# Revit family: O2.5UMA-NRG_Meal Kit
name_source: partatom
category: Mechanical Equipment
revit_build: Autodesk Revit 2017 (Build: 20171027_0315(x64)
units: mm (PartAtom-declared; Revit-internal decimal feet)

## family parameters
Always vertical = Yes
Cut with Voids When Loaded = No
OmniClass Number = 23.40.40.11.17
OmniClass Title = Refrigerated Cases
Part Type = Normal
Room Calculation Point = No
Round Connector Dimension = Use Radius
Shared = No
Work Plane-Based = Yes

## types (37) — shared parameters
11" BF = Yes
ANTI SWEAT APPARENT LOAD = 0 VA
ANTI SWEAT HEATER AMPS = 0 A
ANTI SWEAT HEATER WATTAGE = 0 W
BASE HEIGHT = 5 1/8"
BTU PER FOOT CONVENTIONAL = 857
BTU PER FOOT PARALLEL = 750
CERTIFICATIONS = NSF 7, UL471, CSA
COIL REFRIGERATION CHARGE = 0.00 lb
CONTROL TYPE = T-STAT
DATE = 07/26/12
DEDICATED CIRCUIT = YES
DEFROST AMPS = 0 A
DEFROST PHASE = 1
DEFROST TIME AND DURATION = 2 @ 60 MIN
DEFROST WATTAGE = 0 W
DIEBOARD HEIGHT = 0"
DISCHARGE AIR TEMPERATURE = 31 °F
DRAIN LINE DIAMETER = 2"
DRAIN LINE RADIUS = 1"
DRAIN PIPE TYPE = PVC
DRIP PAN PLUMB TYPE = HARD
Default Elevation = 48"
Defrosts Per Day = 6
Description = MULTI DECK MERCHANDISER WITH SYNERG-E
Discharge Air Velocity (FPM) = 180 FPM
ELECTRIC DEFROST = No
ELECTRICAL DEFROST VOLTAGE = 0 V
EVAPORATOR TEMPERATURE = 28 °F
FAN AMPS = 0 A
FAN NUMBER OF POLES = 1
FAN TYPE = ECM
GROUND FAULT PROTECTION = NO
HEIGHT = 44 1/8"
HOT GAS DEFROST = No
High Efficiency Amps = 0 A
High Power (Cornice) Amps = 0 A
ISOLATED GROUND REQUIRED = NO
Keynote = DAIRY/DELI/MEAT/PRODUCE/SEAFOOD
LED LIGHTING AMPS PER ROW = 0 A
LIGHT TYPE = T8 FLUORESCENT
LIGHTING NUMBER OF POLES = 1
LIQUID LINE DIAMETER = 0"
LIQUID LINE RADIUS = 0"
Manufacturer = HILL PHOENIX
NUMBER OF WIRES = 3
PHASE = 1
POWER FACTOR = 1
PRESSURE REGULATOR = 0.00 psi
RECEPTICAL MOUNTING HEIGHT ABOVE FLOOR = 19 3/4"
REF PLANE FRONT BACK = 21 5/8"
REVERSE AIR DEFROST = No
SET BACK MODE FOR ENERGY CONSERVATION = NO
SHELVE 1 = Yes
SIZE OF COLD WATER HOOK UP = 0"
SIZE OF HOT WATER HOOK-UP = 0"
SUCTION LINE DIAMETER = 1"
SUCTION LINE RADIUS = 0"
Standard Power Amps = 0 A
Superheat Set Point @ Bulb (°F) = 6-8
T8 LIGHT OR LED LIGHT = Yes
TIME OFF DEFROST = Yes
TOEKICK HEIGHT = 5 1/2"
TOEKICK INSET = 1 1/2"
Timed-Off Defrost Fail-Safe (Min) = 30
Timed-Off Defrost Termination Temp = 42 °F
URL = http://www.hillphoenix.com
VOLTAGE = 120 V
WATER LINE MOUNTING HEIGHT ABOVE FLOOR = 0"
WEIGHT = 0.00 lb
WIDTH = 43 1/4"
zero-valued in all types: CORNICE AND NOSE LIGHT ROWS

## per-type parameters (varying)
- 04'-O2.5UMA-NRG-Dairy/Deli/Produce: 5" BF=No; Application Discipline=Meat; BLACK WHEELS=BLACK; BTU ADD FOR LIGHTS=368; BTU ADD PER SHELF PER FOOT=92; BTUH Conventional=847; BTUH Parallel=740; CONVENTIONAL EVAPORATOR LOAD=3796; DRAIN PIPE LENGTH=12"; Discharge Air (°F)=30 °F; EQUIPMENT MARK=O2.5UMA-NRG; Evaporator (°F)=26 °F; FAN AND ANTI SWEAT HEATER APPARENT LOAD=19 VA; FAN APPARENT LOAD=19 VA; FAN QUANTITY=1; FAN WATTAGE=11 W; Front Sill Height=Extended; High Efficiency Watts=11 W; High Power (Cornice) Watts=15 W; LED LIGHTING AMPS=0 A; LED LIGHTING BTU ADD PER ROW=36; LED LIGHTING WATTAGE=12 W; LEGEND NUMBER=O2.5UMA-NRG; LENGTH=48"; LENGTH FOR BTU=4; LIGHT AMPS=0 A; LIGHTING APPARENT LOAD=28 VA; LIGHTING WATTAGE=28 VA; Light Length=4'; Lights Per Row=1; Model=O2.5UMA-NRG; Number of Fans=1; PARALLEL EVAPORATOR LOAD=3368; REF PIPE LENGTH=22 3/4"; REF PLANE LEFT RIGHT=24"; SHELF LIGHT ROWS=1; SHELVE 2=No; SHELVE 3=No; SHELVE LENGTH=48"; Standard Power Watts=6 W; T8 LIGHTING AMPS=0 A; T8 LIGHTING AMPS PER ROW=0 A; T8 LIGHTING BTU ADD PER ROW=92; T8 LIGHTING WATTAGE=28 W; TOTAL APPARENT FAN-LIGHT AND A/S LOAD=39 VA; TOTAL CASE AMPS=0 A; TOTAL CASE WATTAGE=39 W
- 06': 5" BF=Yes; Application Discipline=Dairy/Deli/Produce; BLACK WHEELS=<By Category>; BTU ADD FOR LIGHTS=828; BTU ADD PER SHELF PER FOOT=69; BTUH Conventional=858; BTUH Parallel=750; CONVENTIONAL EVAPORATOR LOAD=5970; DRAIN LINE CONNECTION=Drain Connection; DRAIN PIPE LENGTH=0"; Discharge Air (°F)=31 °F; EQUIPMENT MARK=O2.5UMA-NRG; Evaporator (°F)=28 °F; FAN AND ANTI SWEAT HEATER APPARENT LOAD=38 VA; FAN APPARENT LOAD=38 VA; FAN CONNECTOR DESCRIPTION=FAN AND ANTI SWEAT CONNECTOR; FAN QUANTITY=2; FAN WATTAGE=22 W; Front Sill Height=All; High Efficiency Watts=22 W; High Power (Cornice) Watts=24 W; LED LIGHTING AMPS=0 A; LED LIGHTING BTU ADD PER ROW=27; LED LIGHTING WATTAGE=34 W; LEGEND NUMBER=O2.5UMA-NRG; LENGTH=72"; LENGTH FOR BTU=6; LIGHT AMPS=1 A; LIGHTING APPARENT LOAD=89 VA; LIGHTING CONNECTION DESCRIPTION=LIGHTING CONNECTOR; LIGHTING WATTAGE=89 VA; LIQUID LINE CONNECTION=LIQUID LINE CONNECTION; Light Length=3'; Lights Per Row=2; Model=O2.5UMA-NRG; Number of Fans=2; PARALLEL EVAPORATOR LOAD=5328; REF PIPE LENGTH=28 5/8"; REF PLANE LEFT RIGHT=36"; SHELF LIGHT ROWS=2; SHELVE 2=No; SHELVE 3=Yes; SHELVE LENGTH=36"; SUCTION LINE CONNECTION=SUCTION LINE CONNECTION; Standard Power Watts=9 W; T8 LIGHTING AMPS=1 A; T8 LIGHTING AMPS PER ROW=0 A; T8 LIGHTING BTU ADD PER ROW=69; T8 LIGHTING WATTAGE=89 W; TOTAL APPARENT FAN-LIGHT AND A/S LOAD=111 VA; TOTAL CASE AMPS=1 A; TOTAL CASE WATTAGE=111 W
- 06'-O2.5UMA-NRG- Meat: 5" BF=Yes; Application Discipline=Meat; BLACK WHEELS=<By Category>; BTU ADD FOR LIGHTS=828; BTU ADD PER SHELF PER FOOT=69; BTUH Conventional=847; BTUH Parallel=740; CONVENTIONAL EVAPORATOR LOAD=5970; DRAIN LINE CONNECTION=Drain Connection; DRAIN PIPE LENGTH=0"; Discharge Air (°F)=30 °F; EQUIPMENT MARK=O2.5UMA-NRG; Evaporator (°F)=26 °F; FAN AND ANTI SWEAT HEATER APPARENT LOAD=38 VA; FAN APPARENT LOAD=38 VA; FAN CONNECTOR DESCRIPTION=FAN AND ANTI SWEAT CONNECTOR; FAN QUANTITY=2; FAN WATTAGE=22 W; Front Sill Height=Extended; High Efficiency Watts=22 W; High Power (Cornice) Watts=24 W; LED LIGHTING AMPS=0 A; LED LIGHTING BTU ADD PER ROW=27; LED LIGHTING WATTAGE=34 W; LEGEND NUMBER=O2.5UMA-NRG; LENGTH=72"; LENGTH FOR BTU=6; LIGHT AMPS=1 A; LIGHTING APPARENT LOAD=89 VA; LIGHTING CONNECTION DESCRIPTION=LIGHTING CONNECTOR; LIGHTING WATTAGE=89 VA; LIQUID LINE CONNECTION=LIQUID LINE CONNECTION; Light Length=3'; Lights Per Row=2; Model=O2.5UMA-NRG; Number of Fans=2; PARALLEL EVAPORATOR LOAD=5328; REF PIPE LENGTH=28 5/8"; REF PLANE LEFT RIGHT=36"; SHELF LIGHT ROWS=2; SHELVE 2=No; SHELVE 3=Yes; SHELVE LENGTH=36"; SUCTION LINE CONNECTION=SUCTION LINE CONNECTION; Standard Power Watts=9 W; T8 LIGHTING AMPS=1 A; T8 LIGHTING AMPS PER ROW=0 A; T8 LIGHTING BTU ADD PER ROW=69; T8 LIGHTING WATTAGE=89 W; TOTAL APPARENT FAN-LIGHT AND A/S LOAD=111 VA; TOTAL CASE AMPS=1 A; TOTAL CASE WATTAGE=111 W
- 08': 5" BF=Yes; Application Discipline=Dairy/Deli/Produce; BLACK WHEELS=<By Category>; BTU ADD FOR LIGHTS=1472; BTU ADD PER SHELF PER FOOT=92; BTUH Conventional=858; BTUH Parallel=750; CONVENTIONAL EVAPORATOR LOAD=8328; DRAIN LINE CONNECTION=Drain Connection; DRAIN PIPE LENGTH=0"; Discharge Air (°F)=31 °F; EQUIPMENT MARK=O2.5UMA-NRG; Evaporator (°F)=28 °F; FAN AND ANTI SWEAT HEATER APPARENT LOAD=38 VA; FAN APPARENT LOAD=38 VA; FAN CONNECTOR DESCRIPTION=FAN AND ANTI SWEAT CONNECTOR; FAN QUANTITY=2; FAN WATTAGE=22 W; Front Sill Height=All; High Efficiency Watts=22 W; High Power (Cornice) Watts=30 W; LED LIGHTING AMPS=0 A; LED LIGHTING BTU ADD PER ROW=36; LED LIGHTING WATTAGE=48 W; LEGEND NUMBER=O2.5UMA-NRG; LENGTH=96"; LENGTH FOR BTU=8; LIGHT AMPS=1 A; LIGHTING APPARENT LOAD=113 VA; LIGHTING CONNECTION DESCRIPTION=LIGHTING CONNECTOR; LIGHTING WATTAGE=113 VA; LIQUID LINE CONNECTION=LIQUID LINE CONNECTION; Light Length=4'; Lights Per Row=2; Model=O2.5UMA-NRG; Number of Fans=2; PARALLEL EVAPORATOR LOAD=7472; REF PIPE LENGTH=28 5/8"; REF PLANE LEFT RIGHT=48"; SHELF LIGHT ROWS=2; SHELVE 2=No; SHELVE 3=Yes; SHELVE LENGTH=48"; SUCTION LINE CONNECTION=SUCTION LINE CONNECTION; Standard Power Watts=12 W; T8 LIGHTING AMPS=1 A; T8 LIGHTING AMPS PER ROW=0 A; T8 LIGHTING BTU ADD PER ROW=92; T8 LIGHTING WATTAGE=113 W; TOTAL APPARENT FAN-LIGHT AND A/S LOAD=135 VA; TOTAL CASE AMPS=1 A; TOTAL CASE WATTAGE=135 W
- 08'-O2.5UMA-NRG-Meat: 5" BF=Yes; Application Discipline=Meat`; BLACK WHEELS=<By Category>; BTU ADD FOR LIGHTS=1472; BTU ADD PER SHELF PER FOOT=92; BTUH Conventional=847; BTUH Parallel=740; CONVENTIONAL EVAPORATOR LOAD=8328; DRAIN LINE CONNECTION=Drain Connection; DRAIN PIPE LENGTH=0"; Discharge Air (°F)=30 °F; EQUIPMENT MARK=O2.5UMA-NRG; Evaporator (°F)=26 °F; FAN AND ANTI SWEAT HEATER APPARENT LOAD=38 VA; FAN APPARENT LOAD=38 VA; FAN CONNECTOR DESCRIPTION=FAN AND ANTI SWEAT CONNECTOR; FAN QUANTITY=2; FAN WATTAGE=22 W; Front Sill Height=Extended; High Efficiency Watts=22 W; High Power (Cornice) Watts=30 W; LED LIGHTING AMPS=0 A; LED LIGHTING BTU ADD PER ROW=36; LED LIGHTING WATTAGE=48 W; LEGEND NUMBER=O2.5UM-NRG; LENGTH=96"; LENGTH FOR BTU=8; LIGHT AMPS=1 A; LIGHTING APPARENT LOAD=113 VA; LIGHTING CONNECTION DESCRIPTION=LIGHTING CONNECTOR; LIGHTING WATTAGE=113 VA; LIQUID LINE CONNECTION=LIQUID LINE CONNECTION; Light Length=4'; Lights Per Row=2; Model=O2.5UM-NRG; Number of Fans=2; PARALLEL EVAPORATOR LOAD=7472; REF PIPE LENGTH=28 5/8"; REF PLANE LEFT RIGHT=48"; SHELF LIGHT ROWS=2; SHELVE 2=No; SHELVE 3=Yes; SHELVE LENGTH=48"; SUCTION LINE CONNECTION=SUCTION LINE CONNECTION; Standard Power Watts=12 W; T8 LIGHTING AMPS=1 A; T8 LIGHTING AMPS PER ROW=0 A; T8 LIGHTING BTU ADD PER ROW=92; T8 LIGHTING WATTAGE=113 W; TOTAL APPARENT FAN-LIGHT AND A/S LOAD=135 VA; TOTAL CASE AMPS=1 A; TOTAL CASE WATTAGE=135 W
- 12': 5" BF=Yes; Application Discipline=Dairy/Deli/Produce; BLACK WHEELS=<By Category>; BTU ADD FOR LIGHTS=3312; BTU ADD PER SHELF PER FOOT=92; BTUH Conventional=858; BTUH Parallel=750; CONVENTIONAL EVAPORATOR LOAD=13596; DRAIN LINE CONNECTION=Drain Connection; DRAIN PIPE LENGTH=0"; Discharge Air (°F)=31 °F; EQUIPMENT MARK=O2.5UMA-NRG; Evaporator (°F)=28 °F; FAN AND ANTI SWEAT HEATER APPARENT LOAD=58 VA; FAN APPARENT LOAD=58 VA; FAN CONNECTOR DESCRIPTION=FAN AND ANTI SWEAT CONNECTOR; FAN QUANTITY=3; FAN WATTAGE=33 W; Front Sill Height=All; High Efficiency Watts=33 W; High Power (Cornice) Watts=45 W; LED LIGHTING AMPS=1 A; LED LIGHTING BTU ADD PER ROW=36; LED LIGHTING WATTAGE=108 W; LEGEND NUMBER=O2.5UMA-NRG; LENGTH=144"; LENGTH FOR BTU=12; LIGHT AMPS=2 A; LIGHTING APPARENT LOAD=252 VA; LIGHTING CONNECTION DESCRIPTION=LIGHTING CONNECTOR; LIGHTING WATTAGE=252 VA; LIQUID LINE CONNECTION=LIQUID LINE CONNECTION; Light Length=4'; Lights Per Row=3; Model=O2.5UMA-NRG; Number of Fans=3; PARALLEL EVAPORATOR LOAD=12312; REF PIPE LENGTH=28 5/8"; REF PLANE LEFT RIGHT=72"; SHELF LIGHT ROWS=3; SHELVE 2=Yes; SHELVE 3=Yes; SHELVE LENGTH=48"; SUCTION LINE CONNECTION=SUCTION LINE CONNECTION; Standard Power Watts=18 W; T8 LIGHTING AMPS=2 A; T8 LIGHTING AMPS PER ROW=1 A; T8 LIGHTING BTU ADD PER ROW=92; T8 LIGHTING WATTAGE=252 W; TOTAL APPARENT FAN-LIGHT AND A/S LOAD=285 VA; TOTAL CASE AMPS=3 A; TOTAL CASE WATTAGE=285 W
- 04': 5" BF=No; Application Discipline=Dairy/Deli/Produce; BLACK WHEELS=<By Category>; BTU ADD FOR LIGHTS=368; BTU ADD PER SHELF PER FOOT=92; BTUH Conventional=858; BTUH Parallel=750; CONVENTIONAL EVAPORATOR LOAD=3796; DRAIN LINE CONNECTION=Drain Connection; DRAIN PIPE LENGTH=12"; Discharge Air (°F)=31 °F; EQUIPMENT MARK=O2.5UMA-NRG; Evaporator (°F)=28 °F; FAN AND ANTI SWEAT HEATER APPARENT LOAD=19 VA; FAN APPARENT LOAD=19 VA; FAN CONNECTOR DESCRIPTION=FAN AND ANTI SWEAT CONNECTOR; FAN QUANTITY=1; FAN WATTAGE=11 W; Front Sill Height=All; High Efficiency Watts=11 W; High Power (Cornice) Watts=15 W; LED LIGHTING AMPS=0 A; LED LIGHTING BTU ADD PER ROW=36; LED LIGHTING WATTAGE=12 W; LEGEND NUMBER=O2.5UMA-NRG; LENGTH=48"; LENGTH FOR BTU=4; LIGHT AMPS=0 A; LIGHTING APPARENT LOAD=28 VA; LIGHTING CONNECTION DESCRIPTION=LIGHTING CONNECTOR; LIGHTING WATTAGE=28 VA; LIQUID LINE CONNECTION=LIQUID LINE CONNECTION; Light Length=4'; Lights Per Row=1; Model=O2.5UMA-NRG; Number of Fans=1; PARALLEL EVAPORATOR LOAD=3368; REF PIPE LENGTH=22 3/4"; REF PLANE LEFT RIGHT=24"; SHELF LIGHT ROWS=1; SHELVE 2=No; SHELVE 3=No; SHELVE LENGTH=48"; SUCTION LINE CONNECTION=SUCTION LINE CONNECTION; Standard Power Watts=6 W; T8 LIGHTING AMPS=0 A; T8 LIGHTING AMPS PER ROW=0 A; T8 LIGHTING BTU ADD PER ROW=92; T8 LIGHTING WATTAGE=28 W; TOTAL APPARENT FAN-LIGHT AND A/S LOAD=39 VA; TOTAL CASE AMPS=0 A; TOTAL CASE WATTAGE=39 W
- 06'-O2.5UMA-NRG-Dairy/Deli/Produce: 5" BF=Yes; Application Discipline=Dairy/Deli/Produce; BLACK WHEELS=<By Category>; BTU ADD FOR LIGHTS=828; BTU ADD PER SHELF PER FOOT=69; BTUH Conventional=858; BTUH Parallel=750; CONVENTIONAL EVAPORATOR LOAD=5970; DRAIN LINE CONNECTION=Drain Connection; DRAIN PIPE LENGTH=0"; Discharge Air (°F)=31 °F; EQUIPMENT MARK=O2.5UMA-NRG; Evaporator (°F)=28 °F; FAN AND ANTI SWEAT HEATER APPARENT LOAD=38 VA; FAN APPARENT LOAD=38 VA; FAN CONNECTOR DESCRIPTION=FAN AND ANTI SWEAT CONNECTOR; FAN QUANTITY=2; FAN WATTAGE=22 W; Front Sill Height=All; High Efficiency Watts=22 W; High Power (Cornice) Watts=24 W; LED LIGHTING AMPS=0 A; LED LIGHTING BTU ADD PER ROW=27; LED LIGHTING WATTAGE=34 W; LEGEND NUMBER=O2.5UMA-NRG; LENGTH=72"; LENGTH FOR BTU=6; LIGHT AMPS=1 A; LIGHTING APPARENT LOAD=89 VA; LIGHTING CONNECTION DESCRIPTION=LIGHTING CONNECTOR; LIGHTING WATTAGE=89 VA; LIQUID LINE CONNECTION=LIQUID LINE CONNECTION; Light Length=3'; Lights Per Row=2; Model=O2.5UMA-NRG; Number of Fans=2; PARALLEL EVAPORATOR LOAD=5328; REF PIPE LENGTH=28 5/8"; REF PLANE LEFT RIGHT=36"; SHELF LIGHT ROWS=2; SHELVE 2=No; SHELVE 3=Yes; SHELVE LENGTH=36"; SUCTION LINE CONNECTION=SUCTION LINE CONNECTION; Standard Power Watts=9 W; T8 LIGHTING AMPS=1 A; T8 LIGHTING AMPS PER ROW=0 A; T8 LIGHTING BTU ADD PER ROW=69; T8 LIGHTING WATTAGE=89 W; TOTAL APPARENT FAN-LIGHT AND A/S LOAD=111 VA; TOTAL CASE AMPS=1 A; TOTAL CASE WATTAGE=111 W
- 08'-O2.5UMA-NRG-Dairy/Deli/Produce: 5" BF=Yes; Application Discipline=Dairy/Deli/Produce; BLACK WHEELS=<By Category>; BTU ADD FOR LIGHTS=1472; BTU ADD PER SHELF PER FOOT=92; BTUH Conventional=858; BTUH Parallel=750; CONVENTIONAL EVAPORATOR LOAD=8328; DRAIN LINE CONNECTION=Drain Connection; DRAIN PIPE LENGTH=0"; Discharge Air (°F)=31 °F; EQUIPMENT MARK=O2.5UMA-NRG; Evaporator (°F)=28 °F; FAN AND ANTI SWEAT HEATER APPARENT LOAD=38 VA; FAN APPARENT LOAD=38 VA; FAN CONNECTOR DESCRIPTION=FAN AND ANTI SWEAT CONNECTOR; FAN QUANTITY=2; FAN WATTAGE=22 W; Front Sill Height=All; High Efficiency Watts=22 W; High Power (Cornice) Watts=30 W; LED LIGHTING AMPS=0 A; LED LIGHTING BTU ADD PER ROW=36; LED LIGHTING WATTAGE=48 W; LEGEND NUMBER=O2.5UMA-NRG; LENGTH=96"; LENGTH FOR BTU=8; LIGHT AMPS=1 A; LIGHTING APPARENT LOAD=113 VA; LIGHTING CONNECTION DESCRIPTION=LIGHTING CONNECTOR; LIGHTING WATTAGE=113 VA; LIQUID LINE CONNECTION=LIQUID LINE CONNECTION; Light Length=4'; Lights Per Row=2; Model=O2.5UMA-NRG; Number of Fans=2; PARALLEL EVAPORATOR LOAD=7472; REF PIPE LENGTH=28 5/8"; REF PLANE LEFT RIGHT=48"; SHELF LIGHT ROWS=2; SHELVE 2=No; SHELVE 3=Yes; SHELVE LENGTH=48"; SUCTION LINE CONNECTION=SUCTION LINE CONNECTION; Standard Power Watts=12 W; T8 LIGHTING AMPS=1 A; T8 LIGHTING AMPS PER ROW=0 A; T8 LIGHTING BTU ADD PER ROW=92; T8 LIGHTING WATTAGE=113 W; TOTAL APPARENT FAN-LIGHT AND A/S LOAD=135 VA; TOTAL CASE AMPS=1 A; TOTAL CASE WATTAGE=135 W
- 12'-Dairy/Deli/Produce-O2.5UMA-NRG: 5" BF=Yes; Application Discipline=Dairy/Deli/Produce; BLACK WHEELS=<By Category>; BTU ADD FOR LIGHTS=3312; BTU ADD PER SHELF PER FOOT=92; BTUH Conventional=858; BTUH Parallel=750; CONVENTIONAL EVAPORATOR LOAD=13596; DRAIN LINE CONNECTION=Drain Connection; DRAIN PIPE LENGTH=0"; Discharge Air (°F)=31 °F; EQUIPMENT MARK=O2.5UM-NRG; Evaporator (°F)=28 °F; FAN AND ANTI SWEAT HEATER APPARENT LOAD=58 VA; FAN APPARENT LOAD=58 VA; FAN CONNECTOR DESCRIPTION=FAN AND ANTI SWEAT CONNECTOR; FAN QUANTITY=3; FAN WATTAGE=33 W; Front Sill Height=All; High Efficiency Watts=33 W; High Power (Cornice) Watts=45 W; LED LIGHTING AMPS=1 A; LED LIGHTING BTU ADD PER ROW=36; LED LIGHTING WATTAGE=108 W; LEGEND NUMBER=O2.5UM-NRG; LENGTH=144"; LENGTH FOR BTU=12; LIGHT AMPS=2 A; LIGHTING APPARENT LOAD=252 VA; LIGHTING CONNECTION DESCRIPTION=LIGHTING CONNECTOR; LIGHTING WATTAGE=252 VA; LIQUID LINE CONNECTION=LIQUID LINE CONNECTION; Light Length=4'; Lights Per Row=3; Model=O2.5UM-NRG; Number of Fans=3; PARALLEL EVAPORATOR LOAD=12312; REF PIPE LENGTH=28 5/8"; REF PLANE LEFT RIGHT=72"; SHELF LIGHT ROWS=3; SHELVE 2=Yes; SHELVE 3=Yes; SHELVE LENGTH=48"; SUCTION LINE CONNECTION=SUCTION LINE CONNECTION; Standard Power Watts=18 W; T8 LIGHTING AMPS=2 A; T8 LIGHTING AMPS PER ROW=1 A; T8 LIGHTING BTU ADD PER ROW=92; T8 LIGHTING WATTAGE=252 W; TOTAL APPARENT FAN-LIGHT AND A/S LOAD=285 VA; TOTAL CASE AMPS=3 A; TOTAL CASE WATTAGE=285 W
- 12'-O2.5UMA-NRG-Meat: 5" BF=Yes; Application Discipline=Meat; BLACK WHEELS=<By Category>; BTU ADD FOR LIGHTS=3312; BTU ADD PER SHELF PER FOOT=92; BTUH Conventional=847; BTUH Parallel=740; CONVENTIONAL EVAPORATOR LOAD=13596; DRAIN LINE CONNECTION=Drain Connection; DRAIN PIPE LENGTH=0"; Discharge Air (°F)=30 °F; EQUIPMENT MARK=O2.5UM-NRG; Evaporator (°F)=26 °F; FAN AND ANTI SWEAT HEATER APPARENT LOAD=58 VA; FAN APPARENT LOAD=58 VA; FAN CONNECTOR DESCRIPTION=FAN AND ANTI SWEAT CONNECTOR; FAN QUANTITY=3; FAN WATTAGE=33 W; Front Sill Height=Extended; High Efficiency Watts=33 W; High Power (Cornice) Watts=45 W; LED LIGHTING AMPS=1 A; LED LIGHTING BTU ADD PER ROW=36; LED LIGHTING WATTAGE=108 W; LEGEND NUMBER=O2.5UM-NRG; LENGTH=144"; LENGTH FOR BTU=12; LIGHT AMPS=2 A; LIGHTING APPARENT LOAD=252 VA; LIGHTING CONNECTION DESCRIPTION=LIGHTING CONNECTOR; LIGHTING WATTAGE=252 VA; LIQUID LINE CONNECTION=LIQUID LINE CONNECTION; Light Length=4'; Lights Per Row=3; Model=O2.5UM-NRG; Number of Fans=3; PARALLEL EVAPORATOR LOAD=12312; REF PIPE LENGTH=28 5/8"; REF PLANE LEFT RIGHT=72"; SHELF LIGHT ROWS=3; SHELVE 2=Yes; SHELVE 3=Yes; SHELVE LENGTH=48"; SUCTION LINE CONNECTION=SUCTION LINE CONNECTION; Standard Power Watts=18 W; T8 LIGHTING AMPS=2 A; T8 LIGHTING AMPS PER ROW=1 A; T8 LIGHTING BTU ADD PER ROW=92; T8 LIGHTING WATTAGE=252 W; TOTAL APPARENT FAN-LIGHT AND A/S LOAD=285 VA; TOTAL CASE AMPS=3 A; TOTAL CASE WATTAGE=285 W
- 04'-O2.5UMA-NRG- Meat: 5" BF=No; Application Discipline=Dairy/Deli/Produce; BLACK WHEELS=<By Category>; BTU ADD FOR LIGHTS=368; BTU ADD PER SHELF PER FOOT=92; BTUH Conventional=858; BTUH Parallel=750; CONVENTIONAL EVAPORATOR LOAD=3796; DRAIN LINE CONNECTION=Drain Connection; DRAIN PIPE LENGTH=12"; Discharge Air (°F)=31 °F; EQUIPMENT MARK=O2.5UMA-NRG; Evaporator (°F)=28 °F; FAN AND ANTI SWEAT HEATER APPARENT LOAD=19 VA; FAN APPARENT LOAD=19 VA; FAN CONNECTOR DESCRIPTION=FAN AND ANTI SWEAT CONNECTOR; FAN QUANTITY=1; FAN WATTAGE=11 W; Front Sill Height=All; High Efficiency Watts=11 W; High Power (Cornice) Watts=15 W; LED LIGHTING AMPS=0 A; LED LIGHTING BTU ADD PER ROW=36; LED LIGHTING WATTAGE=12 W; LEGEND NUMBER=O2.5UMA-NRG; LENGTH=48"; LENGTH FOR BTU=4; LIGHT AMPS=0 A; LIGHTING APPARENT LOAD=28 VA; LIGHTING CONNECTION DESCRIPTION=LIGHTING CONNECTOR; LIGHTING WATTAGE=28 VA; LIQUID LINE CONNECTION=LIQUID LINE CONNECTION; Light Length=4'; Lights Per Row=1; Model=O2.5UMA-NRG; Number of Fans=1; PARALLEL EVAPORATOR LOAD=3368; REF PIPE LENGTH=22 3/4"; REF PLANE LEFT RIGHT=24"; SHELF LIGHT ROWS=1; SHELVE 2=No; SHELVE 3=No; SHELVE LENGTH=48"; SUCTION LINE CONNECTION=SUCTION LINE CONNECTION; Standard Power Watts=6 W; T8 LIGHTING AMPS=0 A; T8 LIGHTING AMPS PER ROW=0 A; T8 LIGHTING BTU ADD PER ROW=92; T8 LIGHTING WATTAGE=28 W; TOTAL APPARENT FAN-LIGHT AND A/S LOAD=39 VA; TOTAL CASE AMPS=0 A; TOTAL CASE WATTAGE=39 W
- 12'-O2.5UMNRG-Meat: 5" BF=Yes; Application Discipline=Meat; BLACK WHEELS=<By Category>; BTU ADD FOR LIGHTS=3312; BTU ADD PER SHELF PER FOOT=92; BTUH Conventional=847; BTUH Parallel=740; CONVENTIONAL EVAPORATOR LOAD=13596; DRAIN LINE CONNECTION=Drain Connection; DRAIN PIPE LENGTH=0"; Discharge Air (°F)=30 °F; EQUIPMENT MARK=O2.5UM-NRG; Evaporator (°F)=26 °F; FAN AND ANTI SWEAT HEATER APPARENT LOAD=58 VA; FAN APPARENT LOAD=58 VA; FAN CONNECTOR DESCRIPTION=FAN AND ANTI SWEAT CONNECTOR; FAN QUANTITY=3; FAN WATTAGE=33 W; Front Sill Height=Extended; High Efficiency Watts=33 W; High Power (Cornice) Watts=45 W; LED LIGHTING AMPS=1 A; LED LIGHTING BTU ADD PER ROW=36; LED LIGHTING WATTAGE=108 W; LEGEND NUMBER=O2.5UM-NRG; LENGTH=144"; LENGTH FOR BTU=12; LIGHT AMPS=2 A; LIGHTING APPARENT LOAD=252 VA; LIGHTING CONNECTION DESCRIPTION=LIGHTING CONNECTOR; LIGHTING WATTAGE=252 VA; LIQUID LINE CONNECTION=LIQUID LINE CONNECTION; Light Length=4'; Lights Per Row=3; Model=O2.5UM-NRG; Number of Fans=3; PARALLEL EVAPORATOR LOAD=12312; REF PIPE LENGTH=28 5/8"; REF PLANE LEFT RIGHT=72"; SHELF LIGHT ROWS=3; SHELVE 2=Yes; SHELVE 3=Yes; SHELVE LENGTH=48"; SUCTION LINE CONNECTION=SUCTION LINE CONNECTION; Standard Power Watts=18 W; T8 LIGHTING AMPS=2 A; T8 LIGHTING AMPS PER ROW=1 A; T8 LIGHTING BTU ADD PER ROW=92; T8 LIGHTING WATTAGE=252 W; TOTAL APPARENT FAN-LIGHT AND A/S LOAD=285 VA; TOTAL CASE AMPS=3 A; TOTAL CASE WATTAGE=285 W
- 12'-Dairy/Deli/Produce-O2.5UMNRG: 5" BF=Yes; Application Discipline=Dairy/Deli/Produce; BLACK WHEELS=<By Category>; BTU ADD FOR LIGHTS=3312; BTU ADD PER SHELF PER FOOT=92; BTUH Conventional=858; BTUH Parallel=750; CONVENTIONAL EVAPORATOR LOAD=13596; DRAIN LINE CONNECTION=Drain Connection; DRAIN PIPE LENGTH=0"; Discharge Air (°F)=31 °F; EQUIPMENT MARK=O2.5UM-NRG; Evaporator (°F)=28 °F; FAN AND ANTI SWEAT HEATER APPARENT LOAD=58 VA; FAN APPARENT LOAD=58 VA; FAN CONNECTOR DESCRIPTION=FAN AND ANTI SWEAT CONNECTOR; FAN QUANTITY=3; FAN WATTAGE=33 W; Front Sill Height=All; High Efficiency Watts=33 W; High Power (Cornice) Watts=45 W; LED LIGHTING AMPS=1 A; LED LIGHTING BTU ADD PER ROW=36; LED LIGHTING WATTAGE=108 W; LEGEND NUMBER=O2.5UM-NRG; LENGTH=144"; LENGTH FOR BTU=12; LIGHT AMPS=2 A; LIGHTING APPARENT LOAD=252 VA; LIGHTING CONNECTION DESCRIPTION=LIGHTING CONNECTOR; LIGHTING WATTAGE=252 VA; LIQUID LINE CONNECTION=LIQUID LINE CONNECTION; Light Length=4'; Lights Per Row=3; Model=O2.5UM-NRG; Number of Fans=3; PARALLEL EVAPORATOR LOAD=12312; REF PIPE LENGTH=28 5/8"; REF PLANE LEFT RIGHT=72"; SHELF LIGHT ROWS=3; SHELVE 2=Yes; SHELVE 3=Yes; SHELVE LENGTH=48"; SUCTION LINE CONNECTION=SUCTION LINE CONNECTION; Standard Power Watts=18 W; T8 LIGHTING AMPS=2 A; T8 LIGHTING AMPS PER ROW=1 A; T8 LIGHTING BTU ADD PER ROW=92; T8 LIGHTING WATTAGE=252 W; TOTAL APPARENT FAN-LIGHT AND A/S LOAD=285 VA; TOTAL CASE AMPS=3 A; TOTAL CASE WATTAGE=285 W
- O2.5UM-NRG-12'-5"BF: 5" BF=Yes; Application Discipline=Dairy/Deli/Produce; BLACK WHEELS=<By Category>; BTU ADD FOR LIGHTS=3312; BTU ADD PER SHELF PER FOOT=92; BTUH Conventional=858; BTUH Parallel=750; CONVENTIONAL EVAPORATOR LOAD=13596; DRAIN LINE CONNECTION=Drain Connection; DRAIN PIPE LENGTH=0"; Discharge Air (°F)=31 °F; EQUIPMENT MARK=O2.5UM-NRG; Evaporator (°F)=28 °F; FAN AND ANTI SWEAT HEATER APPARENT LOAD=58 VA; FAN APPARENT LOAD=58 VA; FAN CONNECTOR DESCRIPTION=FAN AND ANTI SWEAT CONNECTOR; FAN QUANTITY=3; FAN WATTAGE=33 W; Front Sill Height=All; High Efficiency Watts=11 W; High Power (Cornice) Watts=15 W; LED LIGHTING AMPS=1 A; LED LIGHTING BTU ADD PER ROW=36; LED LIGHTING WATTAGE=108 W; LEGEND NUMBER=O2.5UM-NRG; LENGTH=144"; LENGTH FOR BTU=12; LIGHT AMPS=2 A; LIGHTING APPARENT LOAD=252 VA; LIGHTING CONNECTION DESCRIPTION=LIGHTING CONNECTOR; LIGHTING WATTAGE=252 VA; LIQUID LINE CONNECTION=LIQUID LINE CONNECTION; Light Length=4'; Lights Per Row=1; Model=O2.5UM-NRG; Number of Fans=1; PARALLEL EVAPORATOR LOAD=12312; REF PIPE LENGTH=28 5/8"; REF PLANE LEFT RIGHT=72"; SHELF LIGHT ROWS=3; SHELVE 2=Yes; SHELVE 3=Yes; SHELVE LENGTH=48"; SUCTION LINE CONNECTION=SUCTION LINE CONNECTION; Standard Power Watts=6 W; T8 LIGHTING AMPS=2 A; T8 LIGHTING AMPS PER ROW=1 A; T8 LIGHTING BTU ADD PER ROW=92; T8 LIGHTING WATTAGE=252 W; TOTAL APPARENT FAN-LIGHT AND A/S LOAD=285 VA; TOTAL CASE AMPS=3 A; TOTAL CASE WATTAGE=285 W
- O2.5UM-NRG-8'-5"BF: 5" BF=Yes; Application Discipline=Dairy/Deli/Produce; BLACK WHEELS=<By Category>; BTU ADD FOR LIGHTS=1472; BTU ADD PER SHELF PER FOOT=92; BTUH Conventional=858; BTUH Parallel=750; CONVENTIONAL EVAPORATOR LOAD=8328; DRAIN LINE CONNECTION=Drain Connection; DRAIN PIPE LENGTH=0"; Discharge Air (°F)=31 °F; EQUIPMENT MARK=O2.5UM-NRG; Evaporator (°F)=28 °F; FAN AND ANTI SWEAT HEATER APPARENT LOAD=38 VA; FAN APPARENT LOAD=38 VA; FAN CONNECTOR DESCRIPTION=FAN AND ANTI SWEAT CONNECTOR; FAN QUANTITY=2; FAN WATTAGE=22 W; Front Sill Height=All; High Efficiency Watts=11 W; High Power (Cornice) Watts=15 W; LED LIGHTING AMPS=0 A; LED LIGHTING BTU ADD PER ROW=36; LED LIGHTING WATTAGE=48 W; LEGEND NUMBER=O2.5UM-NRG; LENGTH=96"; LENGTH FOR BTU=8; LIGHT AMPS=1 A; LIGHTING APPARENT LOAD=113 VA; LIGHTING CONNECTION DESCRIPTION=LIGHTING CONNECTOR; LIGHTING WATTAGE=113 VA; LIQUID LINE CONNECTION=LIQUID LINE CONNECTION; Light Length=4'; Lights Per Row=1; Model=O2.5UM-NRG; Number of Fans=1; PARALLEL EVAPORATOR LOAD=7472; REF PIPE LENGTH=28 5/8"; REF PLANE LEFT RIGHT=48"; SHELF LIGHT ROWS=2; SHELVE 2=No; SHELVE 3=Yes; SHELVE LENGTH=48"; SUCTION LINE CONNECTION=SUCTION LINE CONNECTION; Standard Power Watts=6 W; T8 LIGHTING AMPS=1 A; T8 LIGHTING AMPS PER ROW=0 A; T8 LIGHTING BTU ADD PER ROW=92; T8 LIGHTING WATTAGE=113 W; TOTAL APPARENT FAN-LIGHT AND A/S LOAD=135 VA; TOTAL CASE AMPS=1 A; TOTAL CASE WATTAGE=135 W
- O2.5UM-NRG-6'-5"BF: 5" BF=Yes; Application Discipline=Dairy/Deli/Produce; BLACK WHEELS=<By Category>; BTU ADD FOR LIGHTS=828; BTU ADD PER SHELF PER FOOT=69; BTUH Conventional=858; BTUH Parallel=750; CONVENTIONAL EVAPORATOR LOAD=5970; DRAIN LINE CONNECTION=Drain Connection; DRAIN PIPE LENGTH=0"; Discharge Air (°F)=31 °F; EQUIPMENT MARK=O2.5UM-NRG; Evaporator (°F)=28 °F; FAN AND ANTI SWEAT HEATER APPARENT LOAD=38 VA; FAN APPARENT LOAD=38 VA; FAN CONNECTOR DESCRIPTION=FAN AND ANTI SWEAT CONNECTOR; FAN QUANTITY=2; FAN WATTAGE=22 W; Front Sill Height=All; High Efficiency Watts=11 W; High Power (Cornice) Watts=15 W; LED LIGHTING AMPS=0 A; LED LIGHTING BTU ADD PER ROW=27; LED LIGHTING WATTAGE=34 W; LEGEND NUMBER=O2.5UM-NRG; LENGTH=72"; LENGTH FOR BTU=6; LIGHT AMPS=1 A; LIGHTING APPARENT LOAD=89 VA; LIGHTING CONNECTION DESCRIPTION=LIGHTING CONNECTOR; LIGHTING WATTAGE=89 VA; LIQUID LINE CONNECTION=LIQUID LINE CONNECTION; Light Length=4'; Lights Per Row=1; Model=O2.5UM-NRG; Number of Fans=1; PARALLEL EVAPORATOR LOAD=5328; REF PIPE LENGTH=28 5/8"; REF PLANE LEFT RIGHT=36"; SHELF LIGHT ROWS=2; SHELVE 2=No; SHELVE 3=Yes; SHELVE LENGTH=36"; SUCTION LINE CONNECTION=SUCTION LINE CONNECTION; Standard Power Watts=6 W; T8 LIGHTING AMPS=1 A; T8 LIGHTING AMPS PER ROW=0 A; T8 LIGHTING BTU ADD PER ROW=69; T8 LIGHTING WATTAGE=89 W; TOTAL APPARENT FAN-LIGHT AND A/S LOAD=111 VA; TOTAL CASE AMPS=1 A; TOTAL CASE WATTAGE=111 W
- O2.5UM-NRG-4'-5"BF: 5" BF=No; Application Discipline=Dairy/Deli/Produce; BLACK WHEELS=<By Category>; BTU ADD FOR LIGHTS=368; BTU ADD PER SHELF PER FOOT=92; BTUH Conventional=858; BTUH Parallel=750; CONVENTIONAL EVAPORATOR LOAD=3796; DRAIN LINE CONNECTION=Drain Connection; DRAIN PIPE LENGTH=12"; Discharge Air (°F)=31 °F; EQUIPMENT MARK=O2.5UM-NRG; Evaporator (°F)=28 °F; FAN AND ANTI SWEAT HEATER APPARENT LOAD=19 VA; FAN APPARENT LOAD=19 VA; FAN CONNECTOR DESCRIPTION=FAN AND ANTI SWEAT CONNECTOR; FAN QUANTITY=1; FAN WATTAGE=11 W; Front Sill Height=All; High Efficiency Watts=11 W; High Power (Cornice) Watts=15 W; LED LIGHTING AMPS=0 A; LED LIGHTING BTU ADD PER ROW=36; LED LIGHTING WATTAGE=12 W; LEGEND NUMBER=O2.5UM-NRG; LENGTH=48"; LENGTH FOR BTU=4; LIGHT AMPS=0 A; LIGHTING APPARENT LOAD=28 VA; LIGHTING CONNECTION DESCRIPTION=LIGHTING CONNECTOR; LIGHTING WATTAGE=28 VA; LIQUID LINE CONNECTION=LIQUID LINE CONNECTION; Light Length=4'; Lights Per Row=1; Model=O2.5UM-NRG; Number of Fans=1; PARALLEL EVAPORATOR LOAD=3368; REF PIPE LENGTH=22 3/4"; REF PLANE LEFT RIGHT=24"; SHELF LIGHT ROWS=1; SHELVE 2=No; SHELVE 3=No; SHELVE LENGTH=48"; SUCTION LINE CONNECTION=SUCTION LINE CONNECTION; Standard Power Watts=6 W; T8 LIGHTING AMPS=0 A; T8 LIGHTING AMPS PER ROW=0 A; T8 LIGHTING BTU ADD PER ROW=92; T8 LIGHTING WATTAGE=28 W; TOTAL APPARENT FAN-LIGHT AND A/S LOAD=39 VA; TOTAL CASE AMPS=0 A; TOTAL CASE WATTAGE=39 W
- O2.5UM-NRG-4'-5"BF-Meat: 5" BF=No; Application Discipline=Dairy/Deli/Produce; BLACK WHEELS=<By Category>; BTU ADD FOR LIGHTS=368; BTU ADD PER SHELF PER FOOT=92; BTUH Conventional=858; BTUH Parallel=750; CONVENTIONAL EVAPORATOR LOAD=3796; DRAIN LINE CONNECTION=Drain Connection; DRAIN PIPE LENGTH=12"; Discharge Air (°F)=31 °F; EQUIPMENT MARK=O2.5UM-NRG; Evaporator (°F)=28 °F; FAN AND ANTI SWEAT HEATER APPARENT LOAD=19 VA; FAN APPARENT LOAD=19 VA; FAN CONNECTOR DESCRIPTION=FAN AND ANTI SWEAT CONNECTOR; FAN QUANTITY=1; FAN WATTAGE=11 W; High Efficiency Watts=11 W; High Power (Cornice) Watts=15 W; LED LIGHTING AMPS=0 A; LED LIGHTING BTU ADD PER ROW=36; LED LIGHTING WATTAGE=12 W; LEGEND NUMBER=O2.5UM-NRG; LENGTH=48"; LENGTH FOR BTU=4; LIGHT AMPS=0 A; LIGHTING APPARENT LOAD=28 VA; LIGHTING CONNECTION DESCRIPTION=LIGHTING CONNECTOR; LIGHTING WATTAGE=28 VA; LIQUID LINE CONNECTION=LIQUID LINE CONNECTION; Light Length=4'; Lights Per Row=1; Model=O2.5UM-NRG; Number of Fans=1; PARALLEL EVAPORATOR LOAD=3368; REF PIPE LENGTH=22 3/4"; REF PLANE LEFT RIGHT=24"; SHELF LIGHT ROWS=1; SHELVE 2=No; SHELVE 3=No; SHELVE LENGTH=48"; SUCTION LINE CONNECTION=SUCTION LINE CONNECTION; Standard Power Watts=6 W; T8 LIGHTING AMPS=0 A; T8 LIGHTING AMPS PER ROW=0 A; T8 LIGHTING BTU ADD PER ROW=92; T8 LIGHTING WATTAGE=28 W; TOTAL APPARENT FAN-LIGHT AND A/S LOAD=39 VA; TOTAL CASE AMPS=0 A; TOTAL CASE WATTAGE=39 W
- O2.5UM-NRG-6'-5"BF-Meat: 5" BF=Yes; Application Discipline=Dairy/Deli/Produce; BLACK WHEELS=<By Category>; BTU ADD FOR LIGHTS=828; BTU ADD PER SHELF PER FOOT=69; BTUH Conventional=858; BTUH Parallel=750; CONVENTIONAL EVAPORATOR LOAD=5970; DRAIN LINE CONNECTION=Drain Connection; DRAIN PIPE LENGTH=0"; Discharge Air (°F)=31 °F; EQUIPMENT MARK=O2.5UM-NRG; Evaporator (°F)=28 °F; FAN AND ANTI SWEAT HEATER APPARENT LOAD=38 VA; FAN APPARENT LOAD=38 VA; FAN CONNECTOR DESCRIPTION=FAN AND ANTI SWEAT CONNECTOR; FAN QUANTITY=2; FAN WATTAGE=22 W; Front Sill Height=All; High Efficiency Watts=11 W; High Power (Cornice) Watts=15 W; LED LIGHTING AMPS=0 A; LED LIGHTING BTU ADD PER ROW=27; LED LIGHTING WATTAGE=34 W; LEGEND NUMBER=O2.5UM-NRG; LENGTH=72"; LENGTH FOR BTU=6; LIGHT AMPS=1 A; LIGHTING APPARENT LOAD=89 VA; LIGHTING CONNECTION DESCRIPTION=LIGHTING CONNECTOR; LIGHTING WATTAGE=89 VA; LIQUID LINE CONNECTION=LIQUID LINE CONNECTION; Light Length=4'; Lights Per Row=1; Model=O2.5UM-NRG; Number of Fans=1; PARALLEL EVAPORATOR LOAD=5328; REF PIPE LENGTH=28 5/8"; REF PLANE LEFT RIGHT=36"; SHELF LIGHT ROWS=2; SHELVE 2=No; SHELVE 3=Yes; SHELVE LENGTH=36"; SUCTION LINE CONNECTION=SUCTION LINE CONNECTION; Standard Power Watts=6 W; T8 LIGHTING AMPS=1 A; T8 LIGHTING AMPS PER ROW=0 A; T8 LIGHTING BTU ADD PER ROW=69; T8 LIGHTING WATTAGE=89 W; TOTAL APPARENT FAN-LIGHT AND A/S LOAD=111 VA; TOTAL CASE AMPS=1 A; TOTAL CASE WATTAGE=111 W
- 08'-O2.5UMNRG-Meat: 5" BF=Yes; Application Discipline=Meat`; BLACK WHEELS=<By Category>; BTU ADD FOR LIGHTS=1472; BTU ADD PER SHELF PER FOOT=92; BTUH Conventional=847; BTUH Parallel=740; CONVENTIONAL EVAPORATOR LOAD=8328; DRAIN LINE CONNECTION=Drain Connection; DRAIN PIPE LENGTH=0"; Discharge Air (°F)=30 °F; EQUIPMENT MARK=O2.5UM-NRG; Evaporator (°F)=26 °F; FAN AND ANTI SWEAT HEATER APPARENT LOAD=38 VA; FAN APPARENT LOAD=38 VA; FAN CONNECTOR DESCRIPTION=FAN AND ANTI SWEAT CONNECTOR; FAN QUANTITY=2; FAN WATTAGE=22 W; Front Sill Height=Extended; High Efficiency Watts=22 W; High Power (Cornice) Watts=30 W; LED LIGHTING AMPS=0 A; LED LIGHTING BTU ADD PER ROW=36; LED LIGHTING WATTAGE=48 W; LEGEND NUMBER=O2.5UM-NRG; LENGTH=96"; LENGTH FOR BTU=8; LIGHT AMPS=1 A; LIGHTING APPARENT LOAD=113 VA; LIGHTING CONNECTION DESCRIPTION=LIGHTING CONNECTOR; LIGHTING WATTAGE=113 VA; LIQUID LINE CONNECTION=LIQUID LINE CONNECTION; Light Length=4'; Lights Per Row=2; Model=O2.5UM-NRG; Number of Fans=2; PARALLEL EVAPORATOR LOAD=7472; REF PIPE LENGTH=28 5/8"; REF PLANE LEFT RIGHT=48"; SHELF LIGHT ROWS=2; SHELVE 2=No; SHELVE 3=Yes; SHELVE LENGTH=48"; SUCTION LINE CONNECTION=SUCTION LINE CONNECTION; Standard Power Watts=12 W; T8 LIGHTING AMPS=1 A; T8 LIGHTING AMPS PER ROW=0 A; T8 LIGHTING BTU ADD PER ROW=92; T8 LIGHTING WATTAGE=113 W; TOTAL APPARENT FAN-LIGHT AND A/S LOAD=135 VA; TOTAL CASE AMPS=1 A; TOTAL CASE WATTAGE=135 W
- 06'-O2.5UMNRG-Meat: 5" BF=Yes; Application Discipline=Meat; BLACK WHEELS=<By Category>; BTU ADD FOR LIGHTS=828; BTU ADD PER SHELF PER FOOT=69; BTUH Conventional=847; BTUH Parallel=740; CONVENTIONAL EVAPORATOR LOAD=5970; DRAIN LINE CONNECTION=Drain Connection; DRAIN PIPE LENGTH=0"; Discharge Air (°F)=30 °F; EQUIPMENT MARK=O2.5UM-NRG; Evaporator (°F)=26 °F; FAN AND ANTI SWEAT HEATER APPARENT LOAD=38 VA; FAN APPARENT LOAD=38 VA; FAN CONNECTOR DESCRIPTION=FAN AND ANTI SWEAT CONNECTOR; FAN QUANTITY=2; FAN WATTAGE=22 W; Front Sill Height=Extended; High Efficiency Watts=22 W; High Power (Cornice) Watts=24 W; LED LIGHTING AMPS=0 A; LED LIGHTING BTU ADD PER ROW=27; LED LIGHTING WATTAGE=34 W; LEGEND NUMBER=O2.5UM-NRG; LENGTH=72"; LENGTH FOR BTU=6; LIGHT AMPS=1 A; LIGHTING APPARENT LOAD=89 VA; LIGHTING CONNECTION DESCRIPTION=LIGHTING CONNECTOR; LIGHTING WATTAGE=89 VA; LIQUID LINE CONNECTION=LIQUID LINE CONNECTION; Light Length=3'; Lights Per Row=2; Model=O2.5UM-NRG; Number of Fans=2; PARALLEL EVAPORATOR LOAD=5328; REF PIPE LENGTH=28 5/8"; REF PLANE LEFT RIGHT=36"; SHELF LIGHT ROWS=2; SHELVE 2=No; SHELVE 3=Yes; SHELVE LENGTH=36"; SUCTION LINE CONNECTION=SUCTION LINE CONNECTION; Standard Power Watts=9 W; T8 LIGHTING AMPS=1 A; T8 LIGHTING AMPS PER ROW=0 A; T8 LIGHTING BTU ADD PER ROW=69; T8 LIGHTING WATTAGE=89 W; TOTAL APPARENT FAN-LIGHT AND A/S LOAD=111 VA; TOTAL CASE AMPS=1 A; TOTAL CASE WATTAGE=111 W
- 08'-Dairy/Deli/Produce-O2.5UMNRG: 5" BF=Yes; Application Discipline=Dairy/Deli/Produce; BLACK WHEELS=<By Category>; BTU ADD FOR LIGHTS=1472; BTU ADD PER SHELF PER FOOT=92; BTUH Conventional=858; BTUH Parallel=750; CONVENTIONAL EVAPORATOR LOAD=8328; DRAIN LINE CONNECTION=Drain Connection; DRAIN PIPE LENGTH=0"; Discharge Air (°F)=31 °F; EQUIPMENT MARK=O2.5UM-NRG; Evaporator (°F)=28 °F; FAN AND ANTI SWEAT HEATER APPARENT LOAD=38 VA; FAN APPARENT LOAD=38 VA; FAN CONNECTOR DESCRIPTION=FAN AND ANTI SWEAT CONNECTOR; FAN QUANTITY=2; FAN WATTAGE=22 W; Front Sill Height=All; High Efficiency Watts=22 W; High Power (Cornice) Watts=30 W; LED LIGHTING AMPS=0 A; LED LIGHTING BTU ADD PER ROW=36; LED LIGHTING WATTAGE=48 W; LEGEND NUMBER=O2.5UM-NRG; LENGTH=96"; LENGTH FOR BTU=8; LIGHT AMPS=1 A; LIGHTING APPARENT LOAD=113 VA; LIGHTING CONNECTION DESCRIPTION=LIGHTING CONNECTOR; LIGHTING WATTAGE=113 VA; LIQUID LINE CONNECTION=LIQUID LINE CONNECTION; Light Length=4'; Lights Per Row=2; Model=O2.5UM-NRG; Number of Fans=2; PARALLEL EVAPORATOR LOAD=7472; REF PIPE LENGTH=28 5/8"; REF PLANE LEFT RIGHT=48"; SHELF LIGHT ROWS=2; SHELVE 2=No; SHELVE 3=Yes; SHELVE LENGTH=48"; SUCTION LINE CONNECTION=SUCTION LINE CONNECTION; Standard Power Watts=12 W; T8 LIGHTING AMPS=1 A; T8 LIGHTING AMPS PER ROW=0 A; T8 LIGHTING BTU ADD PER ROW=92; T8 LIGHTING WATTAGE=113 W; TOTAL APPARENT FAN-LIGHT AND A/S LOAD=135 VA; TOTAL CASE AMPS=1 A; TOTAL CASE WATTAGE=135 W
- 06'-Dairy/Deli/Produce-O2.5UMNRG: 5" BF=Yes; Application Discipline=Dairy/Deli/Produce; BLACK WHEELS=<By Category>; BTU ADD FOR LIGHTS=828; BTU ADD PER SHELF PER FOOT=69; BTUH Conventional=858; BTUH Parallel=750; CONVENTIONAL EVAPORATOR LOAD=5970; DRAIN LINE CONNECTION=Drain Connection; DRAIN PIPE LENGTH=0"; Discharge Air (°F)=31 °F; EQUIPMENT MARK=O2.5UM-NRG; Evaporator (°F)=28 °F; FAN AND ANTI SWEAT HEATER APPARENT LOAD=38 VA; FAN APPARENT LOAD=38 VA; FAN CONNECTOR DESCRIPTION=FAN AND ANTI SWEAT CONNECTOR; FAN QUANTITY=2; FAN WATTAGE=22 W; Front Sill Height=All; High Efficiency Watts=22 W; High Power (Cornice) Watts=24 W; LED LIGHTING AMPS=0 A; LED LIGHTING BTU ADD PER ROW=27; LED LIGHTING WATTAGE=34 W; LEGEND NUMBER=O2.5UM-NRG; LENGTH=72"; LENGTH FOR BTU=6; LIGHT AMPS=1 A; LIGHTING APPARENT LOAD=89 VA; LIGHTING CONNECTION DESCRIPTION=LIGHTING CONNECTOR; LIGHTING WATTAGE=89 VA; LIQUID LINE CONNECTION=LIQUID LINE CONNECTION; Light Length=3'; Lights Per Row=2; Model=O2.5UM-NRG; Number of Fans=2; PARALLEL EVAPORATOR LOAD=5328; REF PIPE LENGTH=28 5/8"; REF PLANE LEFT RIGHT=36"; SHELF LIGHT ROWS=2; SHELVE 2=No; SHELVE 3=Yes; SHELVE LENGTH=36"; SUCTION LINE CONNECTION=SUCTION LINE CONNECTION; Standard Power Watts=9 W; T8 LIGHTING AMPS=1 A; T8 LIGHTING AMPS PER ROW=0 A; T8 LIGHTING BTU ADD PER ROW=69; T8 LIGHTING WATTAGE=89 W; TOTAL APPARENT FAN-LIGHT AND A/S LOAD=111 VA; TOTAL CASE AMPS=1 A; TOTAL CASE WATTAGE=111 W
- 04'-Dairy/Deli/Produce-O2.5UMNRG: 5" BF=No; Application Discipline=Dairy/Deli/Produce; BLACK WHEELS=<By Category>; BTU ADD FOR LIGHTS=368; BTU ADD PER SHELF PER FOOT=92; BTUH Conventional=858; BTUH Parallel=750; CONVENTIONAL EVAPORATOR LOAD=3796; DRAIN LINE CONNECTION=Drain Connection; DRAIN PIPE LENGTH=12"; Discharge Air (°F)=31 °F; EQUIPMENT MARK=O2.5UM-NRG; Evaporator (°F)=28 °F; FAN AND ANTI SWEAT HEATER APPARENT LOAD=19 VA; FAN APPARENT LOAD=19 VA; FAN CONNECTOR DESCRIPTION=FAN AND ANTI SWEAT CONNECTOR; FAN QUANTITY=1; FAN WATTAGE=11 W; Front Sill Height=All; High Efficiency Watts=11 W; High Power (Cornice) Watts=15 W; LED LIGHTING AMPS=0 A; LED LIGHTING BTU ADD PER ROW=36; LED LIGHTING WATTAGE=12 W; LEGEND NUMBER=O2.5UM-NRG; LENGTH=48"; LENGTH FOR BTU=4; LIGHT AMPS=0 A; LIGHTING APPARENT LOAD=28 VA; LIGHTING CONNECTION DESCRIPTION=LIGHTING CONNECTOR; LIGHTING WATTAGE=28 VA; LIQUID LINE CONNECTION=LIQUID LINE CONNECTION; Light Length=4'; Lights Per Row=1; Model=O2.5UM-NRG; Number of Fans=1; PARALLEL EVAPORATOR LOAD=3368; REF PIPE LENGTH=22 3/4"; REF PLANE LEFT RIGHT=24"; SHELF LIGHT ROWS=1; SHELVE 2=No; SHELVE 3=No; SHELVE LENGTH=48"; SUCTION LINE CONNECTION=SUCTION LINE CONNECTION; Standard Power Watts=6 W; T8 LIGHTING AMPS=0 A; T8 LIGHTING AMPS PER ROW=0 A; T8 LIGHTING BTU ADD PER ROW=92; T8 LIGHTING WATTAGE=28 W; TOTAL APPARENT FAN-LIGHT AND A/S LOAD=39 VA; TOTAL CASE AMPS=0 A; TOTAL CASE WATTAGE=39 W
- 04'-Meat-O2.5UMNRG: 5" BF=No; Application Discipline=Meat; BLACK WHEELS=<By Category>; BTU ADD FOR LIGHTS=368; BTU ADD PER SHELF PER FOOT=92; BTUH Conventional=847; BTUH Parallel=740; CONVENTIONAL EVAPORATOR LOAD=3796; DRAIN LINE CONNECTION=Drain Connection; DRAIN PIPE LENGTH=12"; Discharge Air (°F)=30 °F; EQUIPMENT MARK=O2.5UM-NRG; Evaporator (°F)=26 °F; FAN AND ANTI SWEAT HEATER APPARENT LOAD=19 VA; FAN APPARENT LOAD=19 VA; FAN CONNECTOR DESCRIPTION=FAN AND ANTI SWEAT CONNECTOR; FAN QUANTITY=1; FAN WATTAGE=11 W; Front Sill Height=Extended; High Efficiency Watts=11 W; High Power (Cornice) Watts=15 W; LED LIGHTING AMPS=0 A; LED LIGHTING BTU ADD PER ROW=36; LED LIGHTING WATTAGE=12 W; LEGEND NUMBER=O2.5UM-NRG; LENGTH=48"; LENGTH FOR BTU=4; LIGHT AMPS=0 A; LIGHTING APPARENT LOAD=28 VA; LIGHTING CONNECTION DESCRIPTION=LIGHTING CONNECTOR; LIGHTING WATTAGE=28 VA; LIQUID LINE CONNECTION=LIQUID LINE CONNECTION; Light Length=4'; Lights Per Row=1; Model=O2.5UM-NRG; Number of Fans=1; PARALLEL EVAPORATOR LOAD=3368; REF PIPE LENGTH=22 3/4"; REF PLANE LEFT RIGHT=24"; SHELF LIGHT ROWS=1; SHELVE 2=No; SHELVE 3=No; SHELVE LENGTH=48"; SUCTION LINE CONNECTION=SUCTION LINE CONNECTION; Standard Power Watts=6 W; T8 LIGHTING AMPS=0 A; T8 LIGHTING AMPS PER ROW=0 A; T8 LIGHTING BTU ADD PER ROW=92; T8 LIGHTING WATTAGE=28 W; TOTAL APPARENT FAN-LIGHT AND A/S LOAD=39 VA; TOTAL CASE AMPS=0 A; TOTAL CASE WATTAGE=39 W
- O2.5UM-NRG-12'-5"BF-Meat: 5" BF=Yes; Application Discipline=Dairy/Deli/Produce; BLACK WHEELS=<By Category>; BTU ADD FOR LIGHTS=3312; BTU ADD PER SHELF PER FOOT=92; BTUH Conventional=858; BTUH Parallel=750; CONVENTIONAL EVAPORATOR LOAD=13596; DRAIN LINE CONNECTION=Drain Connection; DRAIN PIPE LENGTH=0"; Discharge Air (°F)=31 °F; EQUIPMENT MARK=O2.5UM-NRG; Evaporator (°F)=28 °F; FAN AND ANTI SWEAT HEATER APPARENT LOAD=58 VA; FAN APPARENT LOAD=58 VA; FAN CONNECTOR DESCRIPTION=FAN AND ANTI SWEAT CONNECTOR; FAN QUANTITY=3; FAN WATTAGE=33 W; Front Sill Height=All; High Efficiency Watts=11 W; High Power (Cornice) Watts=15 W; LED LIGHTING AMPS=1 A; LED LIGHTING BTU ADD PER ROW=36; LED LIGHTING WATTAGE=108 W; LEGEND NUMBER=O2.5UM-NRG; LENGTH=144"; LENGTH FOR BTU=12; LIGHT AMPS=2 A; LIGHTING APPARENT LOAD=252 VA; LIGHTING CONNECTION DESCRIPTION=LIGHTING CONNECTOR; LIGHTING WATTAGE=252 VA; LIQUID LINE CONNECTION=LIQUID LINE CONNECTION; Light Length=4'; Lights Per Row=1; Model=O2.5UM-NRG; Number of Fans=1; PARALLEL EVAPORATOR LOAD=12312; REF PIPE LENGTH=28 5/8"; REF PLANE LEFT RIGHT=72"; SHELF LIGHT ROWS=3; SHELVE 2=Yes; SHELVE 3=Yes; SHELVE LENGTH=48"; SUCTION LINE CONNECTION=SUCTION LINE CONNECTION; Standard Power Watts=6 W; T8 LIGHTING AMPS=2 A; T8 LIGHTING AMPS PER ROW=1 A; T8 LIGHTING BTU ADD PER ROW=92; T8 LIGHTING WATTAGE=252 W; TOTAL APPARENT FAN-LIGHT AND A/S LOAD=285 VA; TOTAL CASE AMPS=3 A; TOTAL CASE WATTAGE=285 W
- O2.5UM-NRG-8'-5"BF-Meat: 5" BF=Yes; Application Discipline=Dairy/Deli/Produce; BLACK WHEELS=<By Category>; BTU ADD FOR LIGHTS=1472; BTU ADD PER SHELF PER FOOT=92; BTUH Conventional=858; BTUH Parallel=750; CONVENTIONAL EVAPORATOR LOAD=8328; DRAIN LINE CONNECTION=Drain Connection; DRAIN PIPE LENGTH=0"; Discharge Air (°F)=31 °F; EQUIPMENT MARK=O2.5UM-NRG; Evaporator (°F)=28 °F; FAN AND ANTI SWEAT HEATER APPARENT LOAD=38 VA; FAN APPARENT LOAD=38 VA; FAN CONNECTOR DESCRIPTION=FAN AND ANTI SWEAT CONNECTOR; FAN QUANTITY=2; FAN WATTAGE=22 W; Front Sill Height=All; High Efficiency Watts=11 W; High Power (Cornice) Watts=15 W; LED LIGHTING AMPS=0 A; LED LIGHTING BTU ADD PER ROW=36; LED LIGHTING WATTAGE=48 W; LEGEND NUMBER=O2.5UM-NRG; LENGTH=96"; LENGTH FOR BTU=8; LIGHT AMPS=1 A; LIGHTING APPARENT LOAD=113 VA; LIGHTING CONNECTION DESCRIPTION=LIGHTING CONNECTOR; LIGHTING WATTAGE=113 VA; LIQUID LINE CONNECTION=LIQUID LINE CONNECTION; Light Length=4'; Lights Per Row=1; Model=O2.5UM-NRG; Number of Fans=1; PARALLEL EVAPORATOR LOAD=7472; REF PIPE LENGTH=28 5/8"; REF PLANE LEFT RIGHT=48"; SHELF LIGHT ROWS=2; SHELVE 2=No; SHELVE 3=Yes; SHELVE LENGTH=48"; SUCTION LINE CONNECTION=SUCTION LINE CONNECTION; Standard Power Watts=6 W; T8 LIGHTING AMPS=1 A; T8 LIGHTING AMPS PER ROW=0 A; T8 LIGHTING BTU ADD PER ROW=92; T8 LIGHTING WATTAGE=113 W; TOTAL APPARENT FAN-LIGHT AND A/S LOAD=135 VA; TOTAL CASE AMPS=1 A; TOTAL CASE WATTAGE=135 W
- 12' Meat: 5" BF=Yes; Application Discipline=Meat; BLACK WHEELS=<By Category>; BTU ADD FOR LIGHTS=3312; BTU ADD PER SHELF PER FOOT=92; BTUH Conventional=847; BTUH Parallel=740; CONVENTIONAL EVAPORATOR LOAD=13596; DRAIN LINE CONNECTION=Drain Connection; DRAIN PIPE LENGTH=0"; Discharge Air (°F)=30 °F; EQUIPMENT MARK=O2.5UM-NRG; Evaporator (°F)=26 °F; FAN AND ANTI SWEAT HEATER APPARENT LOAD=58 VA; FAN APPARENT LOAD=58 VA; FAN CONNECTOR DESCRIPTION=FAN AND ANTI SWEAT CONNECTOR; FAN QUANTITY=3; FAN WATTAGE=33 W; Front Sill Height=Extended; High Efficiency Watts=33 W; High Power (Cornice) Watts=45 W; LED LIGHTING AMPS=1 A; LED LIGHTING BTU ADD PER ROW=36; LED LIGHTING WATTAGE=108 W; LEGEND NUMBER=O2.5UM-NRG; LENGTH=144"; LENGTH FOR BTU=12; LIGHT AMPS=2 A; LIGHTING APPARENT LOAD=252 VA; LIGHTING CONNECTION DESCRIPTION=LIGHTING CONNECTOR; LIGHTING WATTAGE=252 VA; LIQUID LINE CONNECTION=LIQUID LINE CONNECTION; Light Length=4'; Lights Per Row=3; Model=O2.5UM-NRG; Number of Fans=3; PARALLEL EVAPORATOR LOAD=12312; REF PIPE LENGTH=28 5/8"; REF PLANE LEFT RIGHT=72"; SHELF LIGHT ROWS=3; SHELVE 2=Yes; SHELVE 3=Yes; SHELVE LENGTH=48"; SUCTION LINE CONNECTION=SUCTION LINE CONNECTION; Standard Power Watts=18 W; T8 LIGHTING AMPS=2 A; T8 LIGHTING AMPS PER ROW=1 A; T8 LIGHTING BTU ADD PER ROW=92; T8 LIGHTING WATTAGE=252 W; TOTAL APPARENT FAN-LIGHT AND A/S LOAD=285 VA; TOTAL CASE AMPS=3 A; TOTAL CASE WATTAGE=285 W
- 08' Meat: 5" BF=Yes; Application Discipline=Meat`; BLACK WHEELS=<By Category>; BTU ADD FOR LIGHTS=1472; BTU ADD PER SHELF PER FOOT=92; BTUH Conventional=847; BTUH Parallel=740; CONVENTIONAL EVAPORATOR LOAD=8328; DRAIN LINE CONNECTION=Drain Connection; DRAIN PIPE LENGTH=0"; Discharge Air (°F)=30 °F; EQUIPMENT MARK=O2.5UM-NRG; Evaporator (°F)=26 °F; FAN AND ANTI SWEAT HEATER APPARENT LOAD=38 VA; FAN APPARENT LOAD=38 VA; FAN CONNECTOR DESCRIPTION=FAN AND ANTI SWEAT CONNECTOR; FAN QUANTITY=2; FAN WATTAGE=22 W; Front Sill Height=Extended; High Efficiency Watts=22 W; High Power (Cornice) Watts=30 W; LED LIGHTING AMPS=0 A; LED LIGHTING BTU ADD PER ROW=36; LED LIGHTING WATTAGE=48 W; LEGEND NUMBER=O2.5UM-NRG; LENGTH=96"; LENGTH FOR BTU=8; LIGHT AMPS=1 A; LIGHTING APPARENT LOAD=113 VA; LIGHTING CONNECTION DESCRIPTION=LIGHTING CONNECTOR; LIGHTING WATTAGE=113 VA; LIQUID LINE CONNECTION=LIQUID LINE CONNECTION; Light Length=4'; Lights Per Row=2; Model=O2.5UM-NRG; Number of Fans=2; PARALLEL EVAPORATOR LOAD=7472; REF PIPE LENGTH=28 5/8"; REF PLANE LEFT RIGHT=48"; SHELF LIGHT ROWS=2; SHELVE 2=No; SHELVE 3=Yes; SHELVE LENGTH=48"; SUCTION LINE CONNECTION=SUCTION LINE CONNECTION; Standard Power Watts=12 W; T8 LIGHTING AMPS=1 A; T8 LIGHTING AMPS PER ROW=0 A; T8 LIGHTING BTU ADD PER ROW=92; T8 LIGHTING WATTAGE=113 W; TOTAL APPARENT FAN-LIGHT AND A/S LOAD=135 VA; TOTAL CASE AMPS=1 A; TOTAL CASE WATTAGE=135 W
- 06' Meat: 5" BF=Yes; Application Discipline=Meat; BLACK WHEELS=<By Category>; BTU ADD FOR LIGHTS=828; BTU ADD PER SHELF PER FOOT=69; BTUH Conventional=847; BTUH Parallel=740; CONVENTIONAL EVAPORATOR LOAD=5970; DRAIN LINE CONNECTION=Drain Connection; DRAIN PIPE LENGTH=0"; Discharge Air (°F)=30 °F; EQUIPMENT MARK=O2.5UM-NRG; Evaporator (°F)=26 °F; FAN AND ANTI SWEAT HEATER APPARENT LOAD=38 VA; FAN APPARENT LOAD=38 VA; FAN CONNECTOR DESCRIPTION=FAN AND ANTI SWEAT CONNECTOR; FAN QUANTITY=2; FAN WATTAGE=22 W; Front Sill Height=Extended; High Efficiency Watts=22 W; High Power (Cornice) Watts=24 W; LED LIGHTING AMPS=0 A; LED LIGHTING BTU ADD PER ROW=27; LED LIGHTING WATTAGE=34 W; LEGEND NUMBER=O2.5UM-NRG; LENGTH=72"; LENGTH FOR BTU=6; LIGHT AMPS=1 A; LIGHTING APPARENT LOAD=89 VA; LIGHTING CONNECTION DESCRIPTION=LIGHTING CONNECTOR; LIGHTING WATTAGE=89 VA; LIQUID LINE CONNECTION=LIQUID LINE CONNECTION; Light Length=3'; Lights Per Row=2; Model=O2.5UM-NRG; Number of Fans=2; PARALLEL EVAPORATOR LOAD=5328; REF PIPE LENGTH=28 5/8"; REF PLANE LEFT RIGHT=36"; SHELF LIGHT ROWS=2; SHELVE 2=No; SHELVE 3=Yes; SHELVE LENGTH=36"; SUCTION LINE CONNECTION=SUCTION LINE CONNECTION; Standard Power Watts=9 W; T8 LIGHTING AMPS=1 A; T8 LIGHTING AMPS PER ROW=0 A; T8 LIGHTING BTU ADD PER ROW=69; T8 LIGHTING WATTAGE=89 W; TOTAL APPARENT FAN-LIGHT AND A/S LOAD=111 VA; TOTAL CASE AMPS=1 A; TOTAL CASE WATTAGE=111 W
- 08'  Dairy/Deli/Produce: 5" BF=Yes; Application Discipline=Dairy/Deli/Produce; BLACK WHEELS=<By Category>; BTU ADD FOR LIGHTS=1472; BTU ADD PER SHELF PER FOOT=92; BTUH Conventional=858; BTUH Parallel=750; CONVENTIONAL EVAPORATOR LOAD=8328; DRAIN LINE CONNECTION=Drain Connection; DRAIN PIPE LENGTH=0"; Discharge Air (°F)=31 °F; EQUIPMENT MARK=O2.5UM-NRG; Evaporator (°F)=28 °F; FAN AND ANTI SWEAT HEATER APPARENT LOAD=38 VA; FAN APPARENT LOAD=38 VA; FAN CONNECTOR DESCRIPTION=FAN AND ANTI SWEAT CONNECTOR; FAN QUANTITY=2; FAN WATTAGE=22 W; Front Sill Height=All; High Efficiency Watts=22 W; High Power (Cornice) Watts=30 W; LED LIGHTING AMPS=0 A; LED LIGHTING BTU ADD PER ROW=36; LED LIGHTING WATTAGE=48 W; LEGEND NUMBER=O2.5UM-NRG; LENGTH=96"; LENGTH FOR BTU=8; LIGHT AMPS=1 A; LIGHTING APPARENT LOAD=113 VA; LIGHTING CONNECTION DESCRIPTION=LIGHTING CONNECTOR; LIGHTING WATTAGE=113 VA; LIQUID LINE CONNECTION=LIQUID LINE CONNECTION; Light Length=4'; Lights Per Row=2; Model=O2.5UM-NRG; Number of Fans=2; PARALLEL EVAPORATOR LOAD=7472; REF PIPE LENGTH=28 5/8"; REF PLANE LEFT RIGHT=48"; SHELF LIGHT ROWS=2; SHELVE 2=No; SHELVE 3=Yes; SHELVE LENGTH=48"; SUCTION LINE CONNECTION=SUCTION LINE CONNECTION; Standard Power Watts=12 W; T8 LIGHTING AMPS=1 A; T8 LIGHTING AMPS PER ROW=0 A; T8 LIGHTING BTU ADD PER ROW=92; T8 LIGHTING WATTAGE=113 W; TOTAL APPARENT FAN-LIGHT AND A/S LOAD=135 VA; TOTAL CASE AMPS=1 A; TOTAL CASE WATTAGE=135 W
- 06'  Dairy/Deli/Produce: 5" BF=Yes; Application Discipline=Dairy/Deli/Produce; BLACK WHEELS=<By Category>; BTU ADD FOR LIGHTS=828; BTU ADD PER SHELF PER FOOT=69; BTUH Conventional=858; BTUH Parallel=750; CONVENTIONAL EVAPORATOR LOAD=5970; DRAIN LINE CONNECTION=Drain Connection; DRAIN PIPE LENGTH=0"; Discharge Air (°F)=31 °F; EQUIPMENT MARK=O2.5UM-NRG; Evaporator (°F)=28 °F; FAN AND ANTI SWEAT HEATER APPARENT LOAD=38 VA; FAN APPARENT LOAD=38 VA; FAN CONNECTOR DESCRIPTION=FAN AND ANTI SWEAT CONNECTOR; FAN QUANTITY=2; FAN WATTAGE=22 W; Front Sill Height=All; High Efficiency Watts=22 W; High Power (Cornice) Watts=24 W; LED LIGHTING AMPS=0 A; LED LIGHTING BTU ADD PER ROW=27; LED LIGHTING WATTAGE=34 W; LEGEND NUMBER=O2.5UM-NRG; LENGTH=72"; LENGTH FOR BTU=6; LIGHT AMPS=1 A; LIGHTING APPARENT LOAD=89 VA; LIGHTING CONNECTION DESCRIPTION=LIGHTING CONNECTOR; LIGHTING WATTAGE=89 VA; LIQUID LINE CONNECTION=LIQUID LINE CONNECTION; Light Length=3'; Lights Per Row=2; Model=O2.5UM-NRG; Number of Fans=2; PARALLEL EVAPORATOR LOAD=5328; REF PIPE LENGTH=28 5/8"; REF PLANE LEFT RIGHT=36"; SHELF LIGHT ROWS=2; SHELVE 2=No; SHELVE 3=Yes; SHELVE LENGTH=36"; SUCTION LINE CONNECTION=SUCTION LINE CONNECTION; Standard Power Watts=9 W; T8 LIGHTING AMPS=1 A; T8 LIGHTING AMPS PER ROW=0 A; T8 LIGHTING BTU ADD PER ROW=69; T8 LIGHTING WATTAGE=89 W; TOTAL APPARENT FAN-LIGHT AND A/S LOAD=111 VA; TOTAL CASE AMPS=1 A; TOTAL CASE WATTAGE=111 W
- 04' Dairy/Deli/Produce: 5" BF=No; Application Discipline=Dairy/Deli/Produce; BLACK WHEELS=<By Category>; BTU ADD FOR LIGHTS=368; BTU ADD PER SHELF PER FOOT=92; BTUH Conventional=858; BTUH Parallel=750; CONVENTIONAL EVAPORATOR LOAD=3796; DRAIN LINE CONNECTION=Drain Connection; DRAIN PIPE LENGTH=12"; Discharge Air (°F)=31 °F; EQUIPMENT MARK=O2.5UM-NRG; Evaporator (°F)=28 °F; FAN AND ANTI SWEAT HEATER APPARENT LOAD=19 VA; FAN APPARENT LOAD=19 VA; FAN CONNECTOR DESCRIPTION=FAN AND ANTI SWEAT CONNECTOR; FAN QUANTITY=1; FAN WATTAGE=11 W; Front Sill Height=All; High Efficiency Watts=11 W; High Power (Cornice) Watts=15 W; LED LIGHTING AMPS=0 A; LED LIGHTING BTU ADD PER ROW=36; LED LIGHTING WATTAGE=12 W; LEGEND NUMBER=O2.5UM-NRG; LENGTH=48"; LENGTH FOR BTU=4; LIGHT AMPS=0 A; LIGHTING APPARENT LOAD=28 VA; LIGHTING CONNECTION DESCRIPTION=LIGHTING CONNECTOR; LIGHTING WATTAGE=28 VA; LIQUID LINE CONNECTION=LIQUID LINE CONNECTION; Light Length=4'; Lights Per Row=1; Model=O2.5UM-NRG; Number of Fans=1; PARALLEL EVAPORATOR LOAD=3368; REF PIPE LENGTH=22 3/4"; REF PLANE LEFT RIGHT=24"; SHELF LIGHT ROWS=1; SHELVE 2=No; SHELVE 3=No; SHELVE LENGTH=48"; SUCTION LINE CONNECTION=SUCTION LINE CONNECTION; Standard Power Watts=6 W; T8 LIGHTING AMPS=0 A; T8 LIGHTING AMPS PER ROW=0 A; T8 LIGHTING BTU ADD PER ROW=92; T8 LIGHTING WATTAGE=28 W; TOTAL APPARENT FAN-LIGHT AND A/S LOAD=39 VA; TOTAL CASE AMPS=0 A; TOTAL CASE WATTAGE=39 W
- 12' Dairy/Deli/Produce: 5" BF=Yes; Application Discipline=Dairy/Deli/Produce; BLACK WHEELS=<By Category>; BTU ADD FOR LIGHTS=3312; BTU ADD PER SHELF PER FOOT=92; BTUH Conventional=858; BTUH Parallel=750; CONVENTIONAL EVAPORATOR LOAD=13596; DRAIN LINE CONNECTION=Drain Connection; DRAIN PIPE LENGTH=0"; Discharge Air (°F)=31 °F; EQUIPMENT MARK=O2.5UM-NRG; Evaporator (°F)=28 °F; FAN AND ANTI SWEAT HEATER APPARENT LOAD=58 VA; FAN APPARENT LOAD=58 VA; FAN CONNECTOR DESCRIPTION=FAN AND ANTI SWEAT CONNECTOR; FAN QUANTITY=3; FAN WATTAGE=33 W; Front Sill Height=All; High Efficiency Watts=33 W; High Power (Cornice) Watts=45 W; LED LIGHTING AMPS=1 A; LED LIGHTING BTU ADD PER ROW=36; LED LIGHTING WATTAGE=108 W; LEGEND NUMBER=O2.5UM-NRG; LENGTH=144"; LENGTH FOR BTU=12; LIGHT AMPS=2 A; LIGHTING APPARENT LOAD=252 VA; LIGHTING CONNECTION DESCRIPTION=LIGHTING CONNECTOR; LIGHTING WATTAGE=252 VA; LIQUID LINE CONNECTION=LIQUID LINE CONNECTION; Light Length=4'; Lights Per Row=3; Model=O2.5UM-NRG; Number of Fans=3; PARALLEL EVAPORATOR LOAD=12312; REF PIPE LENGTH=28 5/8"; REF PLANE LEFT RIGHT=72"; SHELF LIGHT ROWS=3; SHELVE 2=Yes; SHELVE 3=Yes; SHELVE LENGTH=48"; SUCTION LINE CONNECTION=SUCTION LINE CONNECTION; Standard Power Watts=18 W; T8 LIGHTING AMPS=2 A; T8 LIGHTING AMPS PER ROW=1 A; T8 LIGHTING BTU ADD PER ROW=92; T8 LIGHTING WATTAGE=252 W; TOTAL APPARENT FAN-LIGHT AND A/S LOAD=285 VA; TOTAL CASE AMPS=3 A; TOTAL CASE WATTAGE=285 W
- 04' Meat: 5" BF=No; Application Discipline=Meat; BLACK WHEELS=<By Category>; BTU ADD FOR LIGHTS=368; BTU ADD PER SHELF PER FOOT=92; BTUH Conventional=847; BTUH Parallel=740; CONVENTIONAL EVAPORATOR LOAD=3796; DRAIN PIPE LENGTH=12"; Discharge Air (°F)=30 °F; EQUIPMENT MARK=O2.5UM-NRG; Evaporator (°F)=26 °F; FAN AND ANTI SWEAT HEATER APPARENT LOAD=19 VA; FAN APPARENT LOAD=19 VA; FAN QUANTITY=1; FAN WATTAGE=11 W; Front Sill Height=Extended; High Efficiency Watts=11 W; High Power (Cornice) Watts=15 W; LED LIGHTING AMPS=0 A; LED LIGHTING BTU ADD PER ROW=36; LED LIGHTING WATTAGE=12 W; LEGEND NUMBER=O2.5UM-NRG; LENGTH=48"; LENGTH FOR BTU=4; LIGHT AMPS=0 A; LIGHTING APPARENT LOAD=28 VA; LIGHTING WATTAGE=28 VA; Light Length=4'; Lights Per Row=1; Model=O2.5UM-NRG; Number of Fans=1; PARALLEL EVAPORATOR LOAD=3368; REF PIPE LENGTH=22 3/4"; REF PLANE LEFT RIGHT=24"; SHELF LIGHT ROWS=1; SHELVE 2=No; SHELVE 3=No; SHELVE LENGTH=48"; Standard Power Watts=6 W; T8 LIGHTING AMPS=0 A; T8 LIGHTING AMPS PER ROW=0 A; T8 LIGHTING BTU ADD PER ROW=92; T8 LIGHTING WATTAGE=28 W; TOTAL APPARENT FAN-LIGHT AND A/S LOAD=39 VA; TOTAL CASE AMPS=0 A; TOTAL CASE WATTAGE=39 W
- 04'-O2.5UMNRG: 5" BF=No; Application Discipline=Meat; BLACK WHEELS=BLACK; BTU ADD FOR LIGHTS=368; BTU ADD PER SHELF PER FOOT=92; BTUH Conventional=847; BTUH Parallel=740; CONVENTIONAL EVAPORATOR LOAD=3796; DRAIN PIPE LENGTH=12"; Discharge Air (°F)=30 °F; EQUIPMENT MARK=O2.5UM-NRG; Evaporator (°F)=26 °F; FAN AND ANTI SWEAT HEATER APPARENT LOAD=19 VA; FAN APPARENT LOAD=19 VA; FAN QUANTITY=1; FAN WATTAGE=11 W; Front Sill Height=Extended; High Efficiency Watts=11 W; High Power (Cornice) Watts=15 W; LED LIGHTING AMPS=0 A; LED LIGHTING BTU ADD PER ROW=36; LED LIGHTING WATTAGE=12 W; LEGEND NUMBER=O2.5UM-NRG; LENGTH=48"; LENGTH FOR BTU=4; LIGHT AMPS=0 A; LIGHTING APPARENT LOAD=28 VA; LIGHTING WATTAGE=28 VA; Light Length=4'; Lights Per Row=1; Model=O2.5UM-NRG; Number of Fans=1; PARALLEL EVAPORATOR LOAD=3368; REF PIPE LENGTH=22 3/4"; REF PLANE LEFT RIGHT=24"; SHELF LIGHT ROWS=1; SHELVE 2=No; SHELVE 3=No; SHELVE LENGTH=48"; Standard Power Watts=6 W; T8 LIGHTING AMPS=0 A; T8 LIGHTING AMPS PER ROW=0 A; T8 LIGHTING BTU ADD PER ROW=92; T8 LIGHTING WATTAGE=28 W; TOTAL APPARENT FAN-LIGHT AND A/S LOAD=39 VA; TOTAL CASE AMPS=0 A; TOTAL CASE WATTAGE=39 W

## geometry (parser evidence)
native form markers: Blend x2, Sweep x9
no freeform markers — native parametric forms only
